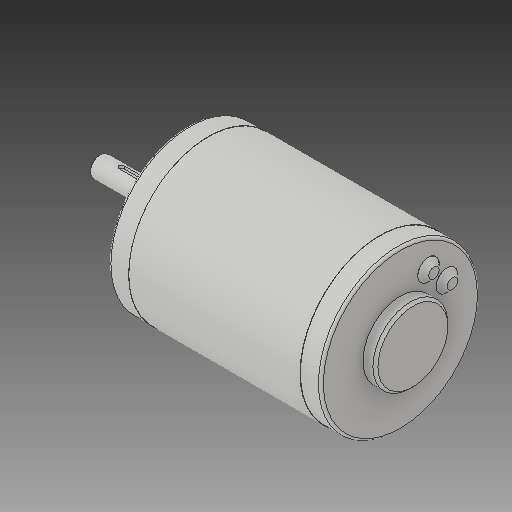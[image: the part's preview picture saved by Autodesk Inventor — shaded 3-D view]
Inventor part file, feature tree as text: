
AUTODESK INVENTOR PART (.ipt)
format: ipt  version: 2017 (Build 210142000, 142)  size: 171,008 bytes
history: native  units: in
note: dims shown in document units (in); Inventor stores cm internally (conversion verified against a paired STEP export)
features: chamfer x1
ambient origin geometry x8: Origin, YZ Plane, XZ Plane, XY Plane, X Axis, Y Axis, Z Axis, Center Point
bodies: Solid1 (feature_tree)
feature tree (1):
  chamfer  "Chamfer3"  [1 undecoded]
note: 1 required parameter value undecoded (feature->parameter linkage not recoverable at this tier; creation-order binding heuristic only, values carry confidence <= 0.55)
